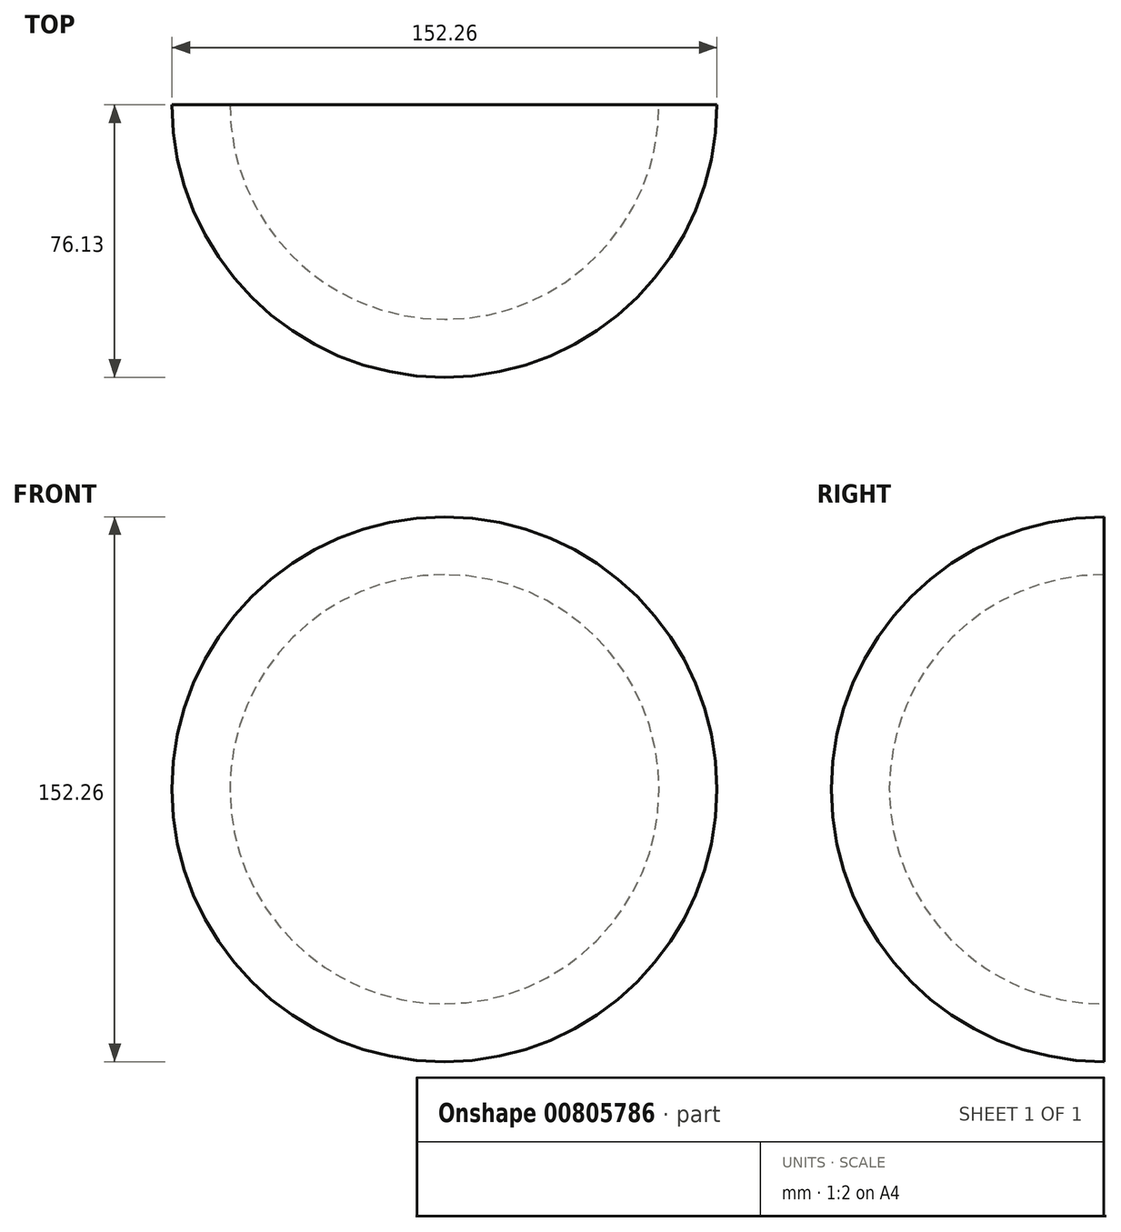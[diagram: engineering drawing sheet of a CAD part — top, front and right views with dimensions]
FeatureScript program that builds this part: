
annotation { "Feature Type Name" : "Feature", "Feature Type Description" : "" }
export const myFeature = defineFeature(function(context is Context, id is Id, definition is map)
    precondition{}
    {
        {
            var Q0;
            Q0=qCreatedBy(makeId("Front.planeOp"),FACE);
            var sketch = newSketch(context, id + "F0", { "sketchPlane" : qUnion([Q0])});
            skCircle(sketch, "E0", {"center": v(0, 0) * mm, "radius": 76.13 * mm});
            skCircle(sketch, "E1", {"center": v(0, 0) * mm, "radius": 37.85 * mm});
            skCircle(sketch, "E2", {"center": v(0, 0) * mm, "radius": 15.68 * mm});
            skCircle(sketch, "E3", {"center": v(0, 0) * mm, "radius": 59.96 * mm});
            skLineSegment(sketch, "E4", {"start": v(0, 0) * mm, "end": v(0, 76.13) * mm});
            skLineSegment(sketch, "E5", {"start": v(0, 0) * mm, "end": v(0, -76.13) * mm});
            skSolve(sketch);
        }
        {
            var Q0;
            {var subQ0=sQuery(id+"F0.wireOp",EDGE,"E4");var subQ1=sQuery(id+"F0.wireOp",EDGE,"E0");var subQ2=makeQuery(id+"F0.imprint","INTERSECT",VERTEX,{"derivedFrom":[subQ1,subQ0]});Q0=makeQuery(id+"F0.imprint","IMPRINT",FACE,{"disambiguationData":[TD([[makeQuery(id+"F0.imprint","IMPRINT",EDGE,{"disambiguationData":[TD([[subQ2,-1.0]])],"derivedFrom":subQ1}),1.0]])]});}
            var Q1;
            Q1=sQuery(id+"F0.wireOp",EDGE,"E4");
            revolve(context, id + "F1", {"surfaceOperationType" : NewSurfaceOperationType.NEW, "entities" : qUnion([Q0]), "axis" : qUnion([Q1]), "revolveType" : RevolveType.ONE_DIRECTION, "angle" : 180 * degree});
        }
    });
